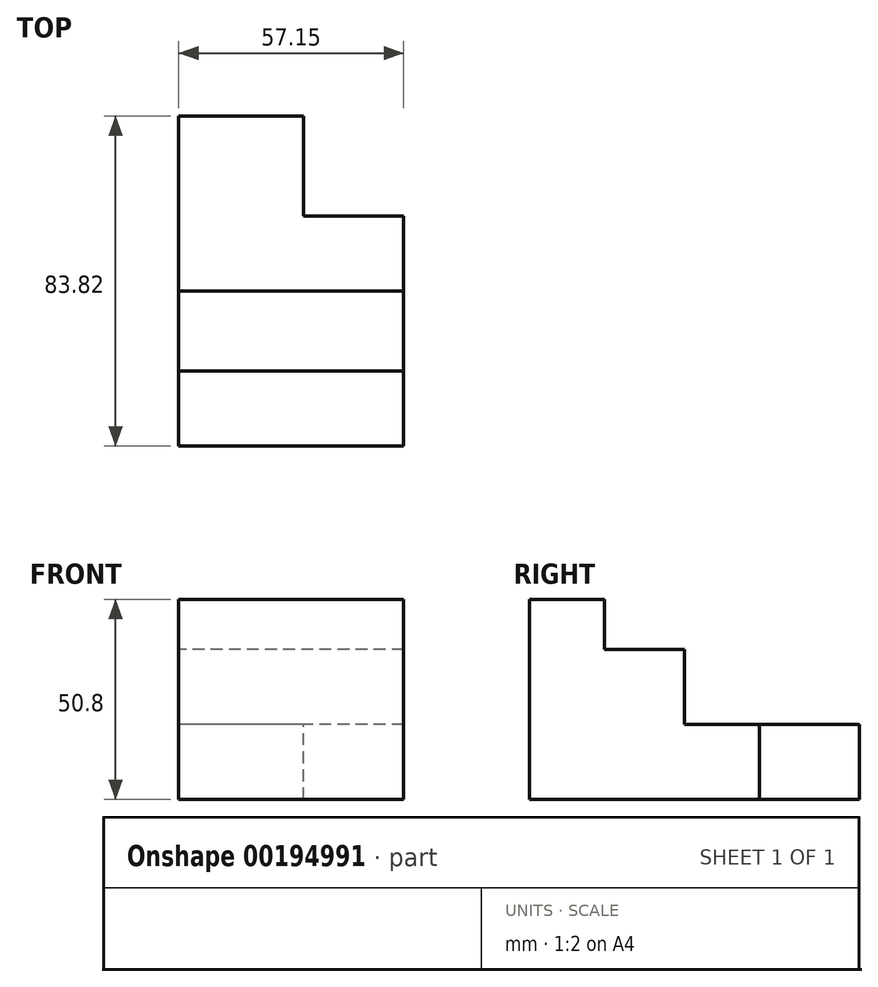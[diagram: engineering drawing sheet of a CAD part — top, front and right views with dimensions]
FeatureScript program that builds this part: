
annotation { "Feature Type Name" : "Feature", "Feature Type Description" : "" }
export const myFeature = defineFeature(function(context is Context, id is Id, definition is map)
    precondition{}
    {
        {
            var Q0;
            Q0=qCreatedBy(makeId("Right.planeOp"),FACE);
            var sketch = newSketch(context, id + "F0", { "sketchPlane" : qUnion([Q0])});
            skLineSegment(sketch, "E0", {"start": v(0, 0) * mm, "end": v(83.82, 0) * mm});
            skLineSegment(sketch, "E1", {"start": v(83.82, 0) * mm, "end": v(83.82, 19.05) * mm});
            skLineSegment(sketch, "E2", {"start": v(83.82, 19.05) * mm, "end": v(39.37, 19.05) * mm});
            skLineSegment(sketch, "E3", {"start": v(39.37, 19.05) * mm, "end": v(39.37, 38.1) * mm});
            skLineSegment(sketch, "E4", {"start": v(39.37, 38.1) * mm, "end": v(19.05, 38.1) * mm});
            skLineSegment(sketch, "E5", {"start": v(19.05, 38.1) * mm, "end": v(19.05, 50.8) * mm});
            skLineSegment(sketch, "E6", {"start": v(19.05, 50.8) * mm, "end": v(0, 50.8) * mm});
            skLineSegment(sketch, "E7", {"start": v(0, 50.8) * mm, "end": v(0, 0) * mm});
            skLineSegment(sketch, "E8", {"start": v(0, 0) * mm, "end": v(0, 0) * mm});
            skSolve(sketch);
        }
        {
            var Q0;
            Q0 = qSketchRegion(id + "F0", true);
            extrude(context, id + "F1", {"entities" : qUnion([Q0]), "depth" : 57.15 * mm});
        }
        {
            var Q0;
            Q0=makeQuery(id+"F1.opExtrude","SWEPT_FACE",FACE,{"disambiguationData":[OSD([sQuery(id+"F0.wireOp",EDGE,"E2")])]});
            var sketch = newSketch(context, id + "F2", { "sketchPlane" : qUnion([Q0])});
            skLineSegment(sketch, "E9.bottom", {"start": v(57.15, 83.82) * mm, "end": v(31.75, 83.82) * mm});
            skLineSegment(sketch, "E9.top", {"start": v(57.15, 58.42) * mm, "end": v(31.75, 58.42) * mm});
            skLineSegment(sketch, "E9.left", {"start": v(57.15, 83.82) * mm, "end": v(57.15, 58.42) * mm});
            skLineSegment(sketch, "E9.right", {"start": v(31.75, 83.82) * mm, "end": v(31.75, 58.42) * mm});
            skSolve(sketch);
        }
        {
            var Q0;
            Q0 = qSketchRegion(id + "F2", true);
            extrude(context, id + "F3", {"entities" : qUnion([Q0]), "operationType" : NewBodyOperationType.REMOVE, "endBound" : BoundingType.THROUGH_ALL, "oppositeDirection" : true, "depth" : 25.4 * mm});
        }
    });
